# Revit family: IS_Conca_T3956_BIM_IT
name_source: partatom
category: Plumbing Fixtures
revit_build: Autodesk Revit 2017 (Build: 20160225_1515(x64)
units: mm (PartAtom-declared; Revit-internal decimal feet)

## family parameters
Always vertical = No
Cut with Voids When Loaded = No
OmniClass Number = 23.45.05.14.21.11
OmniClass Title = Bath/Shower Units
Part Type = Normal
Room Calculation Point = No
Round Connector Dimension = Use Diameter
Shared = No
Work Plane-Based = No

## types (6) — shared parameters
Accessori = https://www.idealstandard.it
Aiuto = https://www.idealstandard.it
AltezzaNominale = 1401 mm  [stored 4.59646 ft]
Autore = Ideal Standard
BIMobject category = Storage
BIMobject category code = sanitary-storage
BIMobject main category = Sanitary
BIMobject main category code = sanitary
Brand = https://www.idealstandard.it
DescrizioneClassifcazioneUni2015 = Bathroom cabinets
DurataGaranzia = 2
DurataGaranziaProdotti = 2
Forma = Rettangolare
Garanzia = Garanzia Idealstandard
IfcEsportaCome = IfcFurnitureType
InformaziniGaranzia = https://www.idealstandard.it
InformazioniDiProdotto = http://www.idealstandard.it
InformazioniGaranzia = https://www.idealstandard.it
Installation instructions = https://www.idealspec.co.uk
InstruzioniInstallazione = https://www.idealstandard.it
LarghezzaNominale = 367 mm  [stored 1.20407 ft]
Maniglia = No
Manufacturer = Ideal Standard
Materiale = Ceramics
NominalDepth = 250 mm  [stored 0.82021 ft]
NominalHeight = 1401 mm  [stored 4.59646 ft]
NominalWidth = 367 mm  [stored 1.20407 ft]
PesoNetto = 29
PiattoDoccia = No
Product group = Bathroom_Furniture
Produttore = Ideal Standard
ProfonditaNominale = 250 mm  [stored 0.82021 ft]
Revisione = 1
RiferimentoClassificazioneUni2015 = Pr_40_30_78_03
Spazio = Interno
Telefono = 800 652 290
TipoEspotazioneIfc = Bathroom cabinets
URL = https://www.ideal-standard.co.uk
Uniclass 2015 Code = Pr_40_30_78_03
Uniclass 2015 Name = Bathroom cabinets
UnitàDurata = Anno
UnitàDurataGaranzia = Anno
UnitàLineare = Milimitre
UnitàMonetaria = €
UnitàSuperficie = Milimitre
UnitàVolume = Litri
Versione = 1
VersioneClassificazioneUni2015 = v1.1
zero-valued in all types: CostoDiSostituzione, DimensioneScarico, LunghezzaNominale, Nominal depth, Nominal height, SeatMaterial, SpessoreDelMateriale, SpilloverLivello, Weight Net (Kg)

## per-type parameters (varying)
| type | Caratteristiche | CodiceABarre | CodiceArticolo | Colore | Description | Desrizione | Finitura | Model | ModelloDiRiferimento | Nome | NomeOggettoBim | NumeroDiModello |
| T3956Y1 - Conca 1/2 COLM  WHMT - T3956 - Y1_MattWhite | Semi colonna 370x250x1400mm dotata di una porta reversibile con sistema di chiusura rallentata e apertura push to open. Dotata di 4 ripiani fissi.Finitura Bianco laccato opaco | 8014140461692 | T3956Y1 | Matt white | Semi column 370x250x1400mm equipped with a reversible door with slow closing system and push to open opening. Equipped with 4 fixed shelves. Matt white lacquered finish | Semi colonna 370x250x1400mm dotata di una porta reversibile con sistema di chiusura rallentata e apertura push to open. Dotata di 4 ripiani fissi.Finitura Bianco laccato opaco | Matt white | T3956Y1 | T3956Y1 | BathroomCabinets_Conca_T3956Y1_IdealStandard | ISI_IdealStandard_Bathroom Cabinets_Conca_T3956Y1 | T3956Y1 |
| T3956Y2 - Conca 1/2 COLM  WHMT - T3956 - Y2_MattAntracite | Semi colonna 370x250x1400mm dotata di una porta reversibile con sistema di chiusura rallentata e apertura push to open. Dotata di 4 ripiani fissi. Finitura Antracite laccato opaco | 8014140461708 | T3956Y2 | Matt anthracite | Semi column 370x250x1400mm equipped with a reversible door with slow closing system and push to open opening. Equipped with 4 fixed shelves. Anthracite matt lacquer finish | Semi colonna 370x250x1400mm dotata di una porta reversibile con sistema di chiusura rallentata e apertura push to open. Dotata di 4 ripiani fissi. Finitura Antracite laccato opaco | Matt anthracite | T3956Y2 | T3956Y2 | BathroomCabinets_Conca_T3956Y2_IdealStandard | ISI_IdealStandard_Bathroom Cabinets_Conca_T3956Y2 | T3956Y2 |
| T3956Y3 - Conca 1/2 COLM  WHMT - T3956 - Y3_MattSunset | Semi colonna 370x250x1400mm dotata di una porta reversibile con sistema di chiusura rallentata e apertura push to open. Dotata di 4 ripiani fissi. Finitura Sunset laccato opaco | 8014140461715 | T3956Y3 | Matt Sunset | Semi column 370x250x1400mm equipped with a reversible door with slow closing system and push to open opening. Equipped with 4 fixed shelves. Sunset matt lacquer finish | Semi colonna 370x250x1400mm dotata di una porta reversibile con sistema di chiusura rallentata e apertura push to open. Dotata di 4 ripiani fissi. Finitura Sunset laccato opaco | Matt Sunset | T3956Y3 | T3956Y3 | BathroomCabinets_Conca_T3956Y3_IdealStandard | ISI_IdealStandard_Bathroom Cabinets_Conca_T3956Y3 | T3956Y3 |
| T3956Y4 - Conca 1/2 COLM  WHMT - T3956 - Y4_SmokedOak | Semi colonna 370x250x1400mm dotata di una porta reversibile con sistema di chiusura rallentata e apertura push to open. Dotata di 4 ripiani fissi. Finitura Rovere affumicato scuro | 8014140461722 | T3956Y4 | Matt Sunset | Semi column 370x250x1400mm equipped with a reversible door with slow closing system and push to open opening. Equipped with 4 fixed shelves. Dark smoked oak finish | Semi colonna 370x250x1400mm dotata di una porta reversibile con sistema di chiusura rallentata e apertura push to open. Dotata di 4 ripiani fissi. Finitura Rovere affumicato scuro | Matt Sunset | T3956Y4 | T3956Y4 | BathroomCabinets_Conca_T3956Y4_IdealStandard | ISI_IdealStandard_Bathroom Cabinets_Conca_T3956Y4 | T3956Y4 |
| T3956Y5 - Conca 1/2 COLM  WHMT - T3956 - Y5_DarkWalnut | Semi colonna 370x250x1400mm dotata di una porta reversibile con sistema di chiusura rallentata e apertura push to open. Dotata di 4 ripiani fissi. Finitura Noce scuro | 8014140461739 | T3956Y5 | Dark Walnut | Semi column 370x250x1400mm equipped with a reversible door with slow closing system and push to open opening. Equipped with 4 fixed shelves. Dark Walnut finish | Semi colonna 370x250x1400mm dotata di una porta reversibile con sistema di chiusura rallentata e apertura push to open. Dotata di 4 ripiani fissi. Finitura Noce scuro | Dark Walnut | T3956Y5 | T3956Y5 | BathroomCabinets_Conca_T3956Y5_IdealStandard | ISI_IdealStandard_Bathroom Cabinets_Conca_T3956Y5 | T3956Y5 |
| T3956Y6 - Conca 1/2 COLM  WHMT - T3956 - Y6_LightOak | Semi colonna 370x250x1400mm dotata di una porta reversibile con sistema di chiusura rallentata e apertura push to open. Dotata di 4 ripiani fissi. Finitura Legno chiaro | 8014140461746 | T3956Y6 | Light Oak | Semi column 370x250x1400mm equipped with a reversible door with slow closing system and push to open opening. Equipped with 4 fixed shelves. Light wood finish | Semi colonna 370x250x1400mm dotata di una porta reversibile con sistema di chiusura rallentata e apertura push to open. Dotata di 4 ripiani fissi. Finitura Legno chiaro | Light Oak | T3956Y6 | T3956Y6 | BathroomCabinets_Conca_T3956Y6_IdealStandard | ISI_IdealStandard_Bathroom Cabinets_Conca_T3956Y6 | T3956Y6 |

note: [stored X ft] marks values corroborated as IEEE doubles in the binary element streams (Revit-internal decimal feet)

## geometry (parser evidence)
native form markers: Sweep x3
no freeform markers — native parametric forms only
